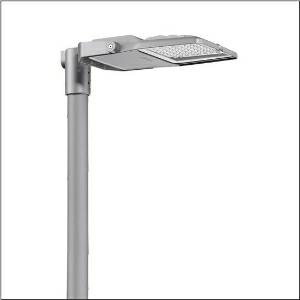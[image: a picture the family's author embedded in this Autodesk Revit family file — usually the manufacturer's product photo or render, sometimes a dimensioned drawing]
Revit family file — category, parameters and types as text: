
# Revit family: floodlight_fl_21_iq_mini___pl61_5xa7772d4c3a_23c5
name_source: partatom
category: Lighting Fixtures
units: mm (PartAtom-declared; Revit-internal decimal feet)

## family parameters
Cut with Voids When Loaded = No
Host = Face
Light Source = No
Part Type = Normal
Room Calculation Point = No
Round Connector Dimension = Use Diameter
Shared = No

## types (1)
- --- (1 x LED, 18260 lm, 143 W, 4000K)
    Apparent Load = 143 VA
    CIE Flux Codes = 33 65 98 100 100
    Color Rendering = 70
    Color Temperature = 4000K
    Default Elevation = 1800 mm
    Description = Floodlight FL 21 iQ mini, floodlight, primary light control with lens, of PMMA, primary optical cover: protective disc, of toughened safety glass, transparent, light distribution: PL61, light emission: direct distribution, installation type: surface-mounted, LED, High Power LED, rated luminous flux: 18.260lm, luminous efficacy: 128lm/W, light colour: 740, colour temperature: 4000K, control gear: iQ Street-Remote/DALI, control: Auto-Match, Temp-Guard, Night-Set, Smart-Wire, Desk-Remote (wireless, voltage-free reading and setting of iQ features in the workshop via application-optimized NFC function/RFID function), optimised constant luminous flux control (CLO 2.0), Light-Fading, Lumen-Switch, with terminal, 6-pole, mains connection: 220..240V, AC, 50/60Hz, start of lifetime: 143W, end of service life: 152W, reduction: 61W, luminaire housing, of diecast aluminium, powder-coated, Siteco® metallic grey (DB 702S), corrosivity category C5 mid according to DIN EN ISO 12944, suitable for swimming pools, chlorine-resistant, sealing non-destructively replaceable, please order mast flange separately, mast bracket, of steel, galvanised, powder-coated, protection rating (complete): IP66, insulation class (complete): insulation class II (safety insulation), certification: CE, ENEC, VDE, protection symbol: D, impact resistance: IK08, permissible operating ambient temperature: -40..+40°C, permissible operating ambient temperature for outdoor applications: -40..+50°C, standard: DIN EN 12944, LABS conformity tested according to VDMA 24364:2018-05, packaging unit: 1 piece

Light Distribution: PL61
    Height = 70 mm
    Lamp = 1 x LED
    Lamp Light Flux = 18260 lm
    Lamp Power = 143 W
    Lamp count = 1
    Length = 485 mm
    Luminous efficacy = 128 lm/W
    Manufacturer = Siteco
    ModVariant = No
    Model = 5XA7772D4C3A
    Number of Poles = 1
    OnlyDefault = Yes
    Power Factor = 1
    Product Name = Floodlight FL 21 iQ mini | PL61
    Product group = floodlight | pylon annexe
    ProductGroupID = 6201
    Protection Class = Protection class II
    Protection Degree = IP 66
    RLX_Detail_Level = 1
    RLX_Emergency_Light_Flux = 0 lm
    RLX_Emergency_Type = 0
    RLX_Emergency_Type_DB = No
    RlxData = <blob elided: 101929 chars, md5=a4cd5408>
    Socket = socket
    Standby Power = 0 W
    System Light Flux = 18260 lm
    System Power = 143 W
    Type Comments = factory setting: luminous flux: 100 % | dim-lin: 254 | 730 mA
    Type Image = l_1007125.jpg
    URL = http://relux.com
    VarID = @adj_193773
    Voltage = 0 V
    Weight = 0.00 kg
    Width = 337 mm

## geometry (parser evidence)
native form markers: Blend x4, Sweep x12
no freeform markers — native parametric forms only
